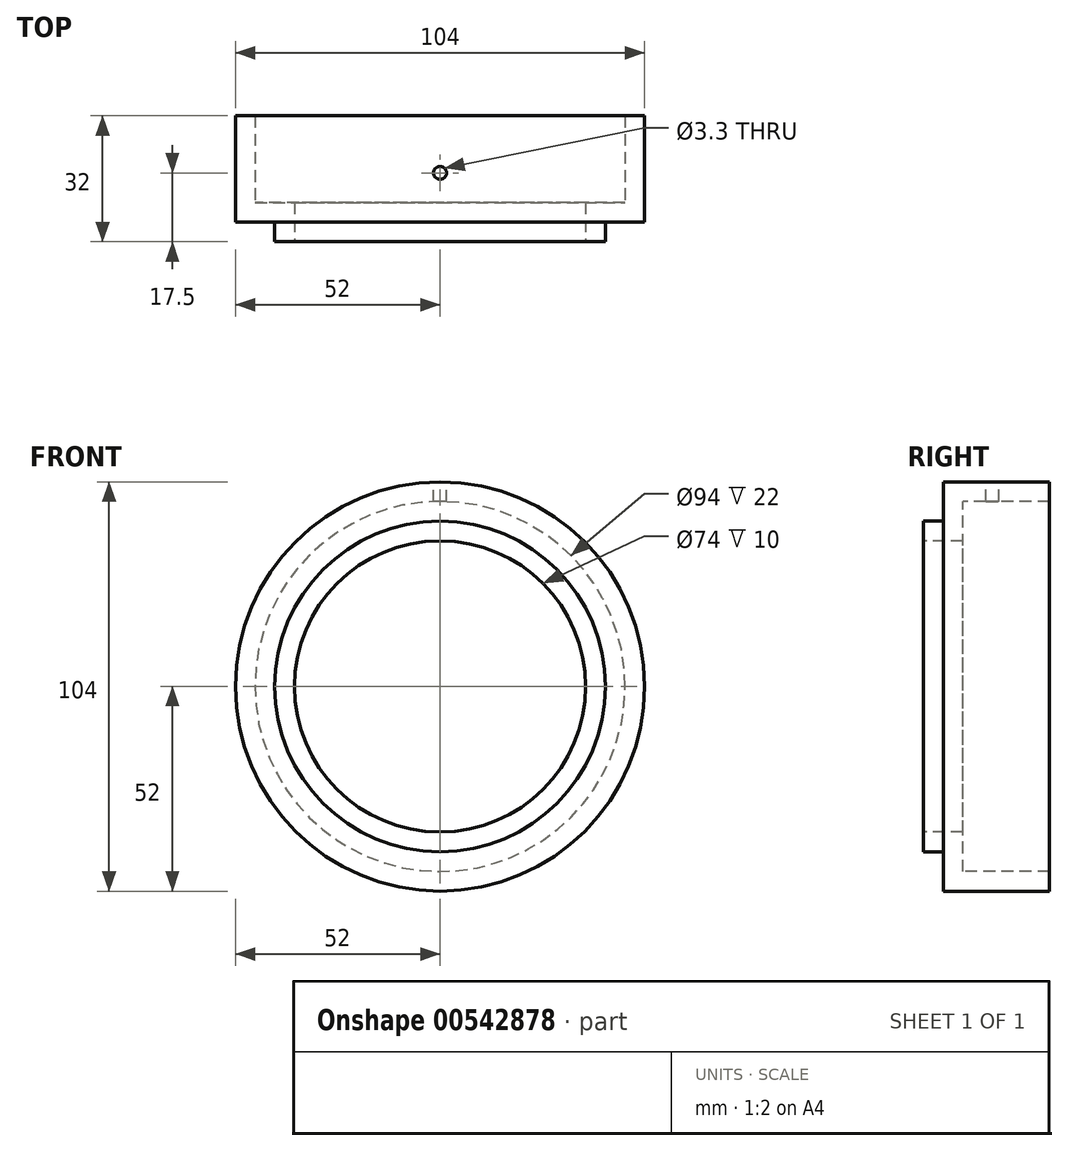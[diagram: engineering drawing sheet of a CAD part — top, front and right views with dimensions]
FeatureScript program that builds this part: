
annotation { "Feature Type Name" : "Feature", "Feature Type Description" : "" }
export const myFeature = defineFeature(function(context is Context, id is Id, definition is map)
    precondition{}
    {
        {
            var Q0;
            Q0=qCreatedBy(makeId("Right.planeOp"),FACE);
            var sketch = newSketch(context, id + "F0", { "sketchPlane" : qUnion([Q0])});
            skLineSegment(sketch, "E0", {"start": v(0, 42) * mm, "end": v(0, 37) * mm});
            skLineSegment(sketch, "E1", {"start": v(0, 37) * mm, "end": v(10, 37) * mm});
            skLineSegment(sketch, "E2", {"start": v(10, 37) * mm, "end": v(10, 47) * mm});
            skLineSegment(sketch, "E3", {"start": v(10, 47) * mm, "end": v(32, 47) * mm});
            skLineSegment(sketch, "E4", {"start": v(32, 47) * mm, "end": v(32, 52) * mm});
            skLineSegment(sketch, "E5", {"start": v(32, 52) * mm, "end": v(5, 52) * mm});
            skLineSegment(sketch, "E6", {"start": v(5, 52) * mm, "end": v(5, 42) * mm});
            skLineSegment(sketch, "E7", {"start": v(5, 42) * mm, "end": v(0, 42) * mm});
            skLineSegment(sketch, "E8", {"start": v(0, 0) * mm, "end": v(50.43, 0) * mm, "construction": true});
            skSolve(sketch);
        }
        {
            var Q0;
            Q0=makeQuery(id+"F0.imprint","IMPRINT",FACE,{"disambiguationData":[TD([[makeQuery(id+"F0.imprint","IMPRINT",EDGE,{"derivedFrom":sQuery(id+"F0.wireOp",EDGE,"E0")}),1.0]])]});
            var Q1;
            Q1=sQuery(id+"F0.wireOp",EDGE,"E8");
            revolve(context, id + "F1", {"entities" : qUnion([Q0]), "axis" : qUnion([Q1]), "revolveType" : RevolveType.FULL});
        }
        {
            var Q0;
            Q0=qCreatedBy(makeId("Right.planeOp"),FACE);
            var sketch = newSketch(context, id + "F2", { "sketchPlane" : qUnion([Q0])});
            skLineSegment(sketch, "E9", {"start": v(32, 47) * mm, "end": v(10, 47) * mm, "construction": true});
            skPoint(sketch, "E10", {"position": v(17.5, 47) * mm});
            skLineSegment(sketch, "E11", {"start": v(32, 52) * mm, "end": v(5, 52) * mm, "construction": true});
            skLineSegment(sketch, "E12", {"start": v(17.5, 47) * mm, "end": v(17.5, 52) * mm, "construction": true});
            skSolve(sketch);
        }
        {
            var Q0;
            Q0=qCreatedBy(makeId("Top.planeOp"),FACE);
            var Q1;
            Q1=sQuery(id+"F2.wireOp",VERTEX,"E12.end");
            cPlane(context, id + "F3", {"entities" : qUnion([Q0, Q1]), "cplaneType" : CPlaneType.PLANE_POINT, "offset" : 25 * mm, "width" : 150 * mm, "height" : 150 * mm});
        }
        {
            var Q0;
            Q0=qCreatedBy(id+"F3.planeOp",FACE);
            var sketch = newSketch(context, id + "F4", { "sketchPlane" : qUnion([Q0])});
            skPoint(sketch, "E13", {"position": v(0, 17.5) * mm});
            skSolve(sketch);
        }
        {
            var Q0;
            Q0=sQuery(id+"F4.wireOp",VERTEX,"E13");
            var Q1;
            Q1=makeQuery(id+"F1.opRevolve","SWEPT_BODY",BODY,{"disambiguationData":[OSD([sQuery(id+"F0.wireOp",EDGE,"E0"),sQuery(id+"F0.wireOp",EDGE,"E1"),sQuery(id+"F0.wireOp",EDGE,"E2"),sQuery(id+"F0.wireOp",EDGE,"E3"),sQuery(id+"F0.wireOp",EDGE,"E4"),sQuery(id+"F0.wireOp",EDGE,"E5"),sQuery(id+"F0.wireOp",EDGE,"E6"),sQuery(id+"F0.wireOp",EDGE,"E7")])]});
            hole(context, id + "F5", {"style" : HoleStyle.SIMPLE, "endStyle" : HoleEndStyle.BLIND, "standardTappedOrClearance" : lookupTablePath({ "standard" : "ISO", "engagement" : "75%", "pitch" : "0.7 mm", "size" : "M4", "type" : "Tapped" }), "standardBlindInLast" : lookupTablePath({ "standard" : "ISO", "engagement" : "75%", "pitch" : "0.7 mm", "size" : "M4", "type" : "Tapped" }), "holeDiameter" : 3.3 * mm, "majorDiameter" : 4 * mm, "showTappedDepth" : true, "holeDepth" : 7.1 * mm, "isTappedThrough" : true, "tappedDepth" : 5 * mm, "tapClearance" : 3, "locations" : qUnion([Q0]), "scope" : qUnion([Q1])});
        }
    });
